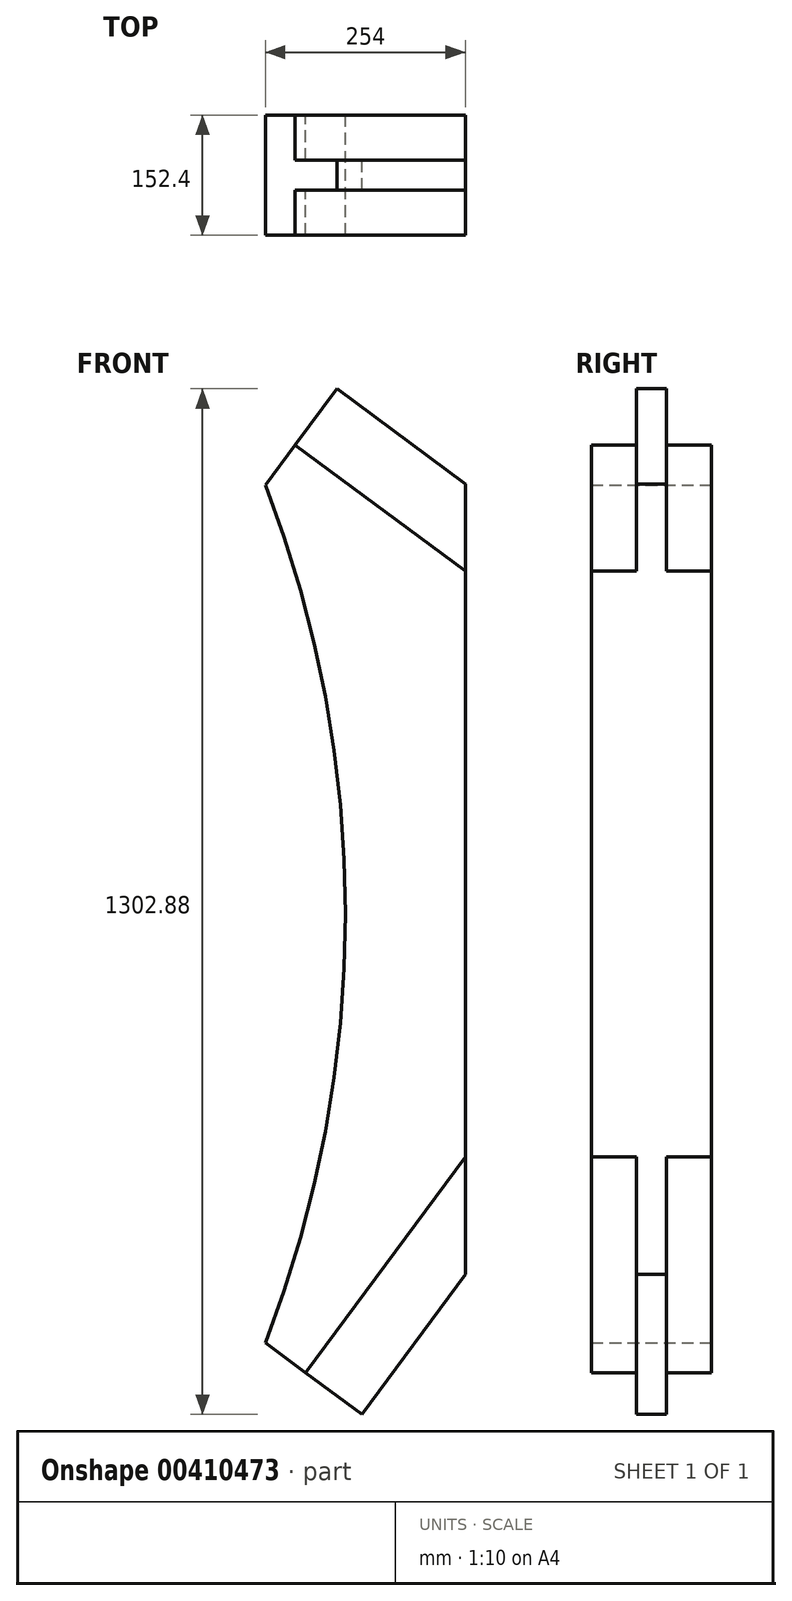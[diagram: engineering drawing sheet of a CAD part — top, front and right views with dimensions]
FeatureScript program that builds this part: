
annotation { "Feature Type Name" : "Feature", "Feature Type Description" : "" }
export const myFeature = defineFeature(function(context is Context, id is Id, definition is map)
    precondition{}
    {
        {
            var Q0;
            Q0=qCreatedBy(makeId("Front.planeOp"),FACE);
            var sketch = newSketch(context, id + "F0", { "sketchPlane" : qUnion([Q0])});
            skLineSegment(sketch, "E0.bottom", {"start": v(-127, 762) * mm, "end": v(127, 762) * mm});
            skLineSegment(sketch, "E0.top", {"start": v(-127, -762) * mm, "end": v(127, -762) * mm});
            skLineSegment(sketch, "E0.left", {"start": v(-127, 762) * mm, "end": v(-127, -762) * mm});
            skLineSegment(sketch, "E0.right", {"start": v(127, 762) * mm, "end": v(127, -762) * mm});
            skPoint(sketch, "E0.middle", {"position": v(0, 0) * mm});
            skLineSegment(sketch, "E1", {"start": v(-127, -562.29) * mm, "end": v(127, -219.39) * mm});
            skLineSegment(sketch, "E2", {"start": v(-127, -562.29) * mm, "end": v(-4.54, -653) * mm});
            skLineSegment(sketch, "E3", {"start": v(-4.54, -653) * mm, "end": v(127, -475.42) * mm});
            skLineSegment(sketch, "E4", {"start": v(127, 339.27) * mm, "end": v(-127, 527.42) * mm});
            skLineSegment(sketch, "E5", {"start": v(-127, 527.42) * mm, "end": v(-36.29, 649.88) * mm});
            skLineSegment(sketch, "E6", {"start": v(-36.29, 649.88) * mm, "end": v(127, 528.93) * mm});
            skLineSegment(sketch, "E7", {"start": v(-96.38, -584.96) * mm, "end": v(127, -283.4) * mm});
            skLineSegment(sketch, "E8", {"start": v(-104.32, 558.04) * mm, "end": v(127, 386.69) * mm});
            skLineSegment(sketch, "E9", {"start": v(-75.97, -600.08) * mm, "end": v(127, -326.07) * mm});
            skLineSegment(sketch, "E10", {"start": v(-89.2, 578.45) * mm, "end": v(127, 418.3) * mm});
            skArc(sketch, "E11", {"start": v(-127, -562.29) * mm, "mid": v(-25.4, -17.43) * mm, "end": v(-127, 527.42) * mm});
            skSolve(sketch);
        }
        {
            var Q0;
            {var subQ0=sQuery(id+"F0.wireOp",EDGE,"E1");Q0=makeQuery(id+"F0.imprint","IMPRINT",FACE,{"disambiguationData":[TD([[makeQuery(id+"F0.imprint","IMPRINT",EDGE,{"derivedFrom":subQ0}),1.0]])]});}
            var Q1;
            {var subQ0=sQuery(id+"F0.wireOp",EDGE,"E1");Q1=makeQuery(id+"F0.imprint","IMPRINT",FACE,{"disambiguationData":[TD([[makeQuery(id+"F0.imprint","IMPRINT",EDGE,{"derivedFrom":subQ0}),-1.0]])]});}
            var Q2;
            {var subQ0=sQuery(id+"F0.wireOp",EDGE,"E4");Q2=makeQuery(id+"F0.imprint","IMPRINT",FACE,{"disambiguationData":[TD([[makeQuery(id+"F0.imprint","IMPRINT",EDGE,{"derivedFrom":subQ0}),-1.0]])]});}
            var Q3;
            {var subQ0=sQuery(id+"F0.wireOp",EDGE,"E7");Q3=makeQuery(id+"F0.imprint","IMPRINT",FACE,{"disambiguationData":[TD([[makeQuery(id+"F0.imprint","IMPRINT",EDGE,{"derivedFrom":subQ0}),-1.0]])]});}
            var Q4;
            {var subQ0=sQuery(id+"F0.wireOp",EDGE,"E8");Q4=makeQuery(id+"F0.imprint","IMPRINT",FACE,{"disambiguationData":[TD([[makeQuery(id+"F0.imprint","IMPRINT",EDGE,{"derivedFrom":subQ0}),1.0]])]});}
            extrude(context, id + "F1", {"entities" : qUnion([Q0, Q1, Q2, Q3, Q4]), "depth" : 152.4 * mm, "offsetDistance" : 25.4 * mm, "symmetric" : true});
        }
        {
            var Q0;
            {var subQ2=sQuery(id+"F0.wireOp",EDGE,"E3");Q0=makeQuery(id+"F0.imprint","IMPRINT",FACE,{"disambiguationData":[TD([[makeQuery(id+"F0.imprint","IMPRINT",EDGE,{"derivedFrom":subQ2}),1.0]])]});}
            var Q1;
            {var subQ5=sQuery(id+"F0.wireOp",EDGE,"pFaVbikq-wH3B-tn6S-bqlM-S9TkdjifRTJL");Q1=makeQuery(id+"F0.imprint","IMPRINT",FACE,{"disambiguationData":[TD([[makeQuery(id+"F0.imprint","IMPRINT",EDGE,{"derivedFrom":subQ5}),-1.0]])]});}
            var Q2;
            {var subQ0=sQuery(id+"F0.wireOp",EDGE,"r5AdvcZR-K32a-sbp1-snoH-I1G2CRFFrvgr");Q2=makeQuery(id+"F0.imprint","IMPRINT",FACE,{"disambiguationData":[TD([[makeQuery(id+"F0.imprint","IMPRINT",EDGE,{"derivedFrom":subQ0}),1.0]])]});}
            var Q3;
            {var subQ0=sQuery(id+"F0.wireOp",EDGE,"E6");Q3=makeQuery(id+"F0.imprint","IMPRINT",FACE,{"disambiguationData":[TD([[makeQuery(id+"F0.imprint","IMPRINT",EDGE,{"derivedFrom":subQ0}),-1.0]])]});}
            extrude(context, id + "F2", {"entities" : qUnion([Q0, Q1, Q2, Q3]), "operationType" : NewBodyOperationType.ADD, "depth" : 38.1 * mm, "offsetDistance" : 25.4 * mm, "symmetric" : true});
        }
    });
